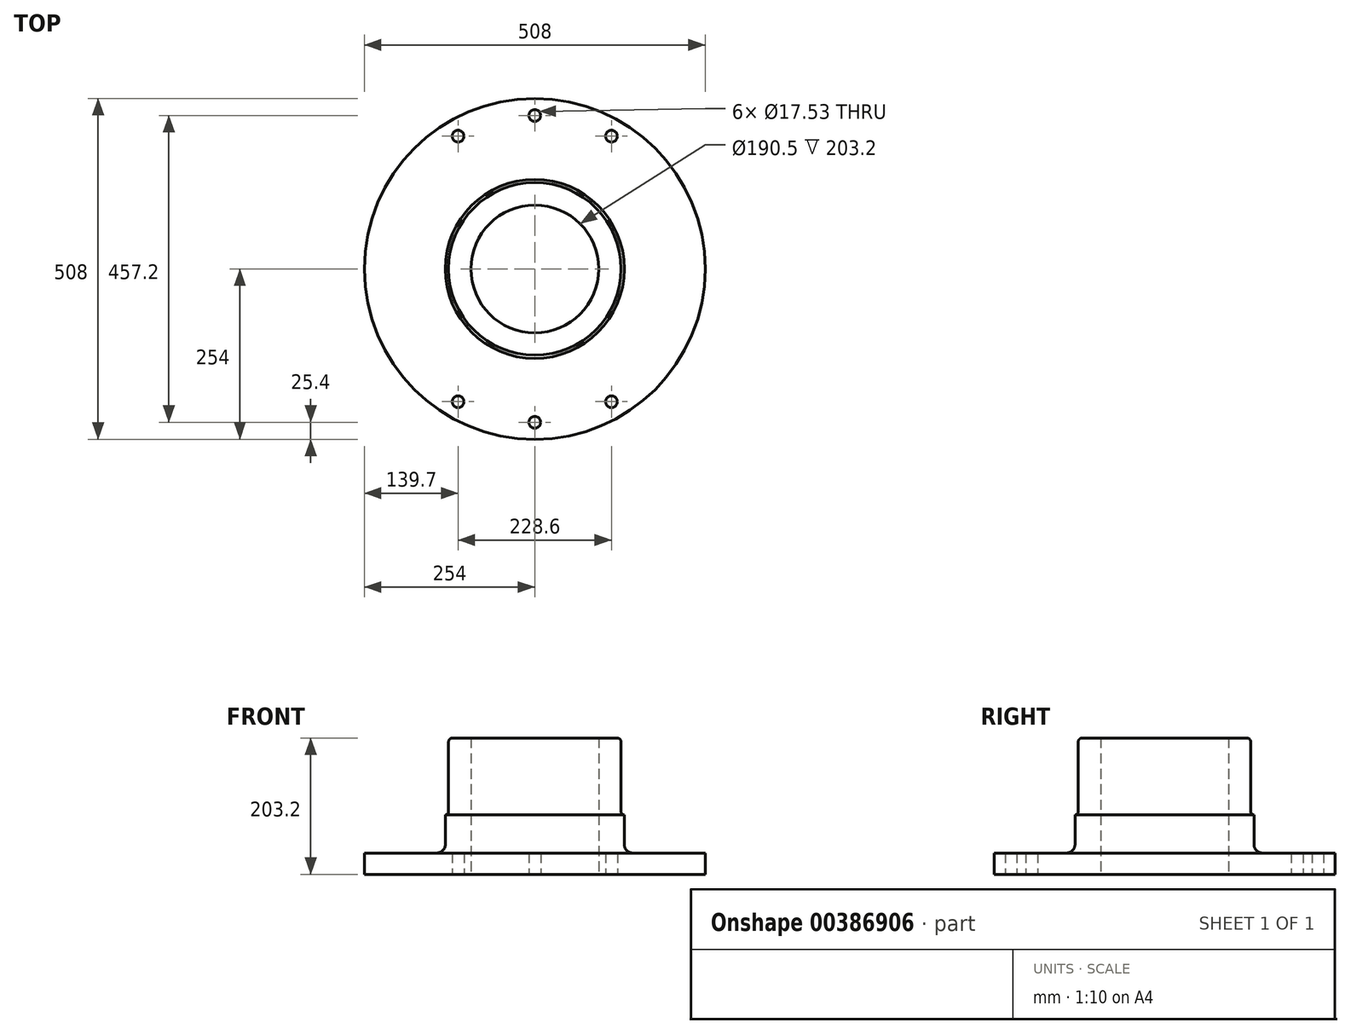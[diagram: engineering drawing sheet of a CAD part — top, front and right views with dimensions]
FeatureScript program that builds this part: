
annotation { "Feature Type Name" : "Feature", "Feature Type Description" : "" }
export const myFeature = defineFeature(function(context is Context, id is Id, definition is map)
    precondition{}
    {
        {
            var Q0;
            Q0=qCreatedBy(makeId("Front.planeOp"),FACE);
            var sketch = newSketch(context, id + "F0", { "sketchPlane" : qUnion([Q0])});
            skLineSegment(sketch, "E0", {"start": v(95.25, 0) * mm, "end": v(95.25, 203.2) * mm});
            skLineSegment(sketch, "E1", {"start": v(95.25, 203.2) * mm, "end": v(122.3, 203.2) * mm});
            skLineSegment(sketch, "E2", {"start": v(128.65, 196.85) * mm, "end": v(128.65, 92.9) * mm});
            skLineSegment(sketch, "E3", {"start": v(132.65, 88.9) * mm, "end": v(133.35, 88.9) * mm});
            skLineSegment(sketch, "E4", {"start": v(133.35, 88.9) * mm, "end": v(133.35, 44.45) * mm});
            skLineSegment(sketch, "E5", {"start": v(146.05, 31.75) * mm, "end": v(254, 31.75) * mm});
            skLineSegment(sketch, "E6", {"start": v(254, 31.75) * mm, "end": v(254, 0) * mm});
            skLineSegment(sketch, "E7", {"start": v(254, 0) * mm, "end": v(95.25, 0) * mm});
            skPoint(sketch, "E8.visualSharp", {"position": v(133.35, 31.75) * mm});
            skArc(sketch, "E8.filletArc", {"start": v(133.35, 44.45) * mm, "mid": v(137.07, 35.47) * mm, "end": v(146.05, 31.75) * mm});
            skPoint(sketch, "E9.visualSharp", {"position": v(128.65, 88.9) * mm});
            skArc(sketch, "E9.filletArc", {"start": v(128.65, 92.9) * mm, "mid": v(129.82, 90.07) * mm, "end": v(132.65, 88.9) * mm});
            skPoint(sketch, "E10.visualSharp", {"position": v(128.65, 203.2) * mm});
            skArc(sketch, "E10.filletArc", {"start": v(128.65, 196.85) * mm, "mid": v(126.8, 201.34) * mm, "end": v(122.3, 203.2) * mm});
            skLineSegment(sketch, "E11", {"start": v(0, 0) * mm, "end": v(0, 244.68) * mm, "construction": true});
            skSolve(sketch);
        }
        {
            var Q0;
            Q0 = qSketchRegion(id + "F0", true);
            var Q1;
            Q1=sQuery(id+"F0.wireOp",EDGE,"E11");
            revolve(context, id + "F1", {"entities" : qUnion([Q0]), "axis" : qUnion([Q1]), "revolveType" : RevolveType.FULL});
        }
        {
            var Q0;
            Q0=qCreatedBy(makeId("Top.planeOp"),FACE);
            var sketch = newSketch(context, id + "F2", { "sketchPlane" : qUnion([Q0])});
            skCircle(sketch, "E12", {"center": v(0, 228.6) * mm, "radius": 8.76 * mm});
            skCircle(sketch, "E13", {"center": v(0, -228.6) * mm, "radius": 8.76 * mm});
            skCircle(sketch, "E14", {"center": v(114.3, -197.87) * mm, "radius": 8.76 * mm});
            skCircle(sketch, "E15", {"center": v(-114.3, -197.87) * mm, "radius": 8.76 * mm});
            skCircle(sketch, "E16", {"center": v(-114.3, 197.87) * mm, "radius": 8.76 * mm});
            skCircle(sketch, "E17", {"center": v(114.3, 197.87) * mm, "radius": 8.76 * mm});
            skSolve(sketch);
        }
        {
            var Q0;
            Q0 = qSketchRegion(id + "F2", true);
            extrude(context, id + "F3", {"entities" : qUnion([Q0]), "operationType" : NewBodyOperationType.REMOVE, "endBound" : BoundingType.THROUGH_ALL, "depth" : 25 * mm, "offsetDistance" : 25 * mm});
        }
    });
